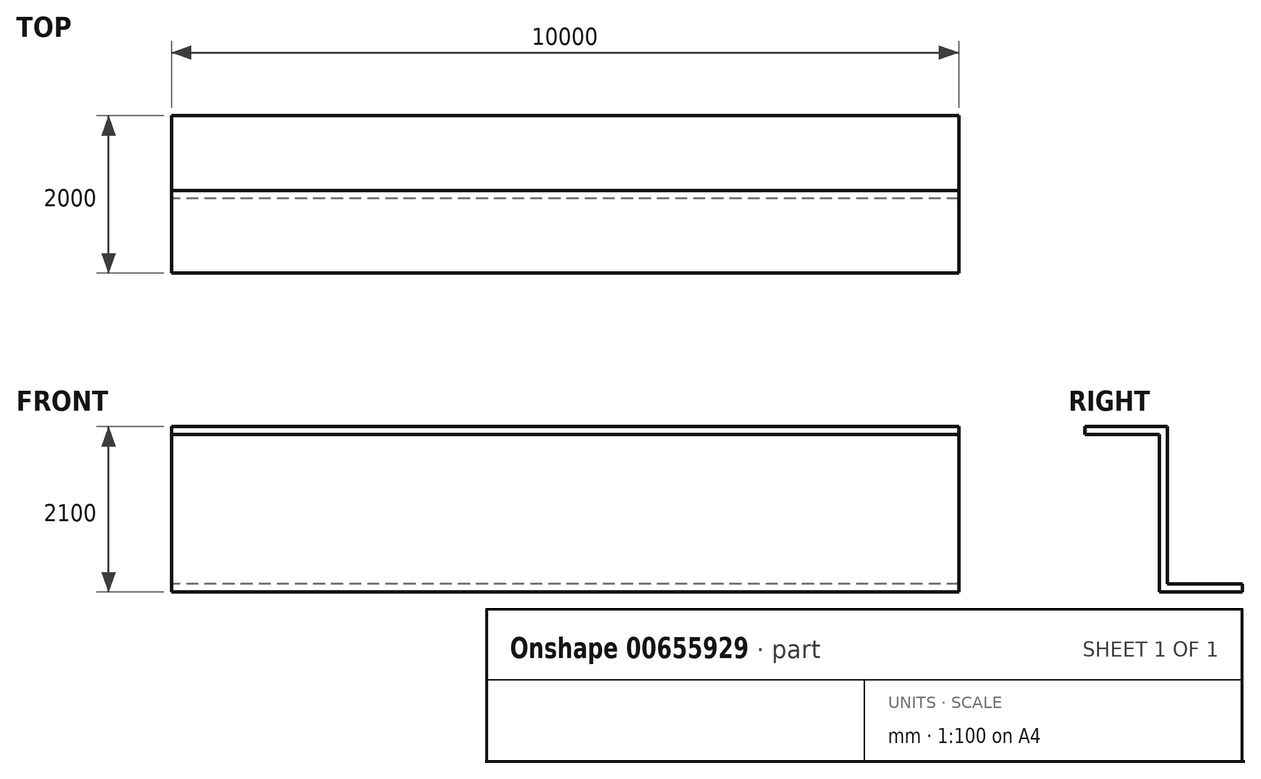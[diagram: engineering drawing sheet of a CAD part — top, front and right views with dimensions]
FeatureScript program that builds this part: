
annotation { "Feature Type Name" : "Feature", "Feature Type Description" : "" }
export const myFeature = defineFeature(function(context is Context, id is Id, definition is map)
    precondition{}
    {
        {
            var Q0;
            Q0=qCreatedBy(makeId("Right.planeOp"),FACE);
            var sketch = newSketch(context, id + "F0", { "sketchPlane" : qUnion([Q0])});
            skLineSegment(sketch, "E0.0", {"start": v(50, 1050) * mm, "end": v(-1000, 1050) * mm});
            skLineSegment(sketch, "E0.1", {"start": v(50, 0) * mm, "end": v(50, 1050) * mm});
            skLineSegment(sketch, "E0.2", {"start": v(50, 0) * mm, "end": v(50, -950) * mm});
            skLineSegment(sketch, "E0.3", {"start": v(50, -950) * mm, "end": v(1000, -950) * mm});
            skLineSegment(sketch, "E1.0", {"start": v(-50, 950) * mm, "end": v(-1000, 950) * mm});
            skLineSegment(sketch, "E1.1", {"start": v(-50, 0) * mm, "end": v(-50, 950) * mm});
            skLineSegment(sketch, "E1.2", {"start": v(-50, 0) * mm, "end": v(-50, -1050) * mm});
            skLineSegment(sketch, "E1.3", {"start": v(-50, -1050) * mm, "end": v(1000, -1050) * mm});
            skLineSegment(sketch, "E2", {"start": v(-1000, 1050) * mm, "end": v(-1000, 950) * mm});
            skLineSegment(sketch, "E3", {"start": v(1000, -950) * mm, "end": v(1000, -1050) * mm});
            skSolve(sketch);
        }
        {
            var Q0;
            Q0=qSketchRegion(id+"F0",true);
            var Q1;
            Q1=qConstructionFilter(qBodyType(qCreatedBy(id+"F0",EDGE),BodyType.WIRE),ConstructionObject.NO);
            extrude(context, id + "F1", {"entities" : qUnion([Q0]), "surfaceEntities" : qUnion([Q1]), "depth" : 10000 * mm, "offsetDistance" : 25 * mm});
        }
    });
